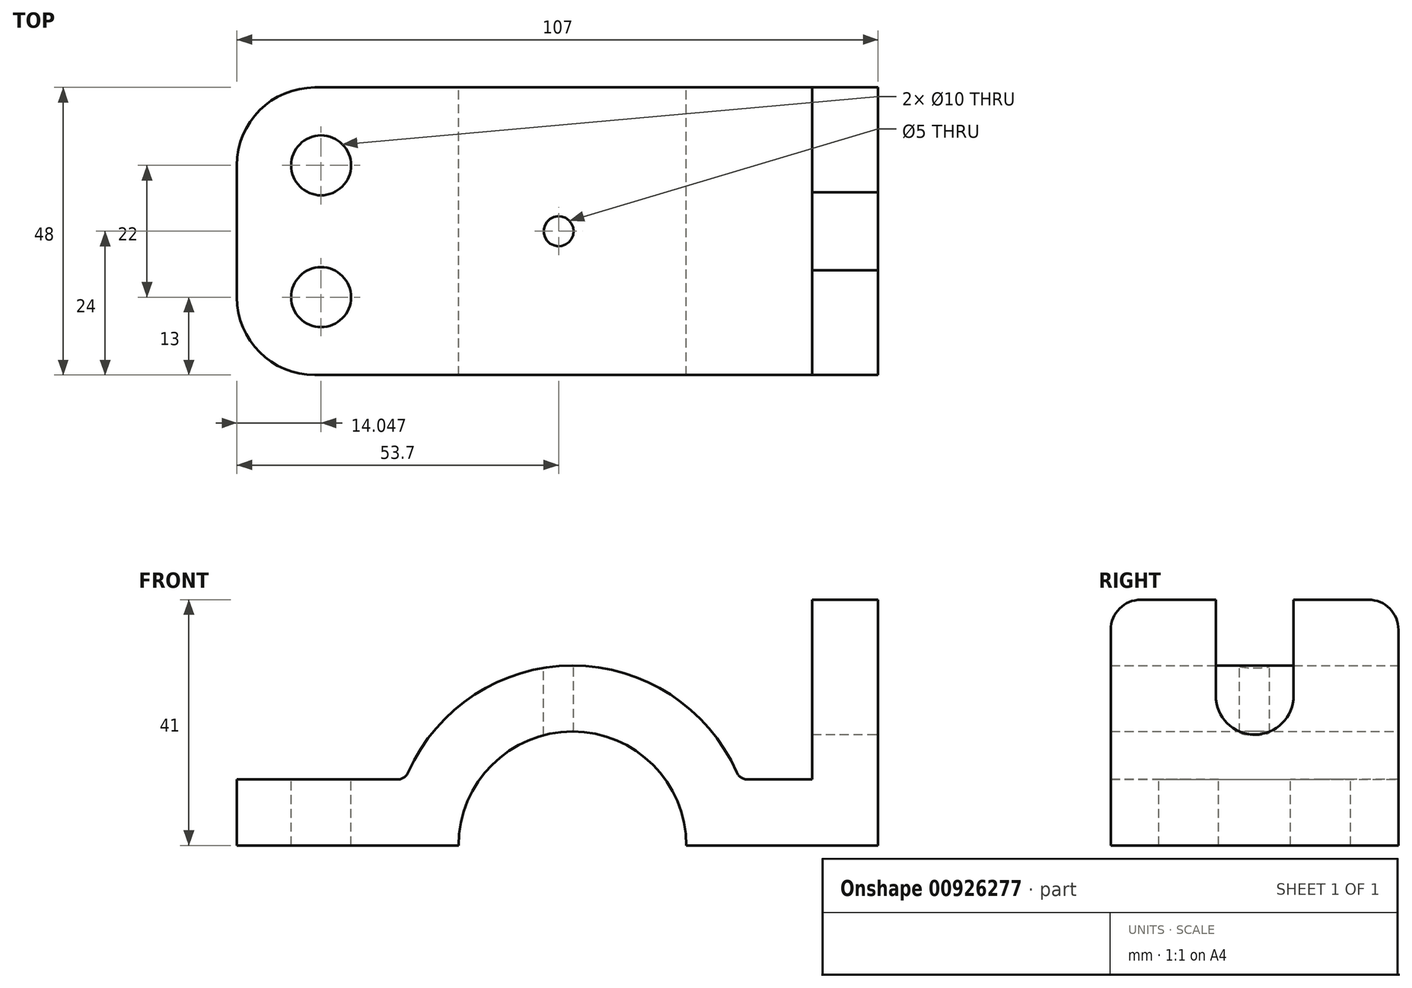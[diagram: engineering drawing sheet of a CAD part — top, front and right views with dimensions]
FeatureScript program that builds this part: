
annotation { "Feature Type Name" : "Feature", "Feature Type Description" : "" }
export const myFeature = defineFeature(function(context is Context, id is Id, definition is map)
    precondition{}
    {
        {
            var Q0;
            Q0=qCreatedBy(makeId("Front.planeOp"),FACE);
            var sketch = newSketch(context, id + "F0", { "sketchPlane" : qUnion([Q0])});
            skLineSegment(sketch, "E0.bottom", {"start": v(-53.7, -8.93) * mm, "end": v(53.3, -8.93) * mm});
            skLineSegment(sketch, "E0.top", {"start": v(-53.7, -19.93) * mm, "end": v(53.3, -19.93) * mm});
            skLineSegment(sketch, "E0.left", {"start": v(-53.7, -8.93) * mm, "end": v(-53.7, -19.93) * mm});
            skLineSegment(sketch, "E0.right", {"start": v(53.3, -8.93) * mm, "end": v(53.3, -19.93) * mm});
            skPoint(sketch, "E1", {"position": v(2.3, -19.93) * mm});
            skCircle(sketch, "E2", {"center": v(2.3, -19.93) * mm, "radius": 30 * mm});
            skCircle(sketch, "E3", {"center": v(2.3, -19.93) * mm, "radius": 19 * mm});
            skLineSegment(sketch, "E4.bottom", {"start": v(42.3, 21.07) * mm, "end": v(53.3, 21.07) * mm});
            skLineSegment(sketch, "E4.top", {"start": v(42.3, -8.93) * mm, "end": v(53.3, -8.93) * mm});
            skLineSegment(sketch, "E4.left", {"start": v(42.3, 21.07) * mm, "end": v(42.3, -8.93) * mm});
            skLineSegment(sketch, "E4.right", {"start": v(53.3, 21.07) * mm, "end": v(53.3, -8.93) * mm});
            skSolve(sketch);
        }
        {
            var Q0;
            {var subQ0=sQuery(id+"F0.wireOp",EDGE,"E0.left");Q0=makeQuery(id+"F0.imprint","IMPRINT",FACE,{"disambiguationData":[TD([[makeQuery(id+"F0.imprint","IMPRINT",EDGE,{"derivedFrom":subQ0}),1.0]])]});}
            var Q1;
            {var subQ0=sQuery(id+"F0.wireOp",EDGE,"E2");var subQ1=sQuery(id+"F0.wireOp",EDGE,"E0.bottom");var subQ2=makeQuery(id+"F0.imprint","INTERSECT",VERTEX,{"disambiguationData":[OD(0.0)],"derivedFrom":[subQ1,subQ0]});Q1=makeQuery(id+"F0.imprint","IMPRINT",FACE,{"disambiguationData":[TD([[makeQuery(id+"F0.imprint","IMPRINT",EDGE,{"disambiguationData":[TD([[subQ2,-1.0]])],"derivedFrom":subQ1}),-1.0]])]});}
            var Q2;
            {var subQ0=sQuery(id+"F0.wireOp",EDGE,"E2");var subQ1=sQuery(id+"F0.wireOp",EDGE,"E0.bottom");var subQ2=makeQuery(id+"F0.imprint","INTERSECT",VERTEX,{"disambiguationData":[OD(0.0)],"derivedFrom":[subQ1,subQ0]});Q2=makeQuery(id+"F0.imprint","IMPRINT",FACE,{"disambiguationData":[TD([[makeQuery(id+"F0.imprint","IMPRINT",EDGE,{"disambiguationData":[TD([[subQ2,-1.0]])],"derivedFrom":subQ1}),1.0]])]});}
            var Q3;
            {var subQ0=sQuery(id+"F0.wireOp",EDGE,"E2");var subQ1=sQuery(id+"F0.wireOp",EDGE,"E0.bottom");var subQ2=makeQuery(id+"F0.imprint","INTERSECT",VERTEX,{"disambiguationData":[OD(1.0)],"derivedFrom":[subQ1,subQ0]});Q3=makeQuery(id+"F0.imprint","IMPRINT",FACE,{"disambiguationData":[TD([[makeQuery(id+"F0.imprint","IMPRINT",EDGE,{"disambiguationData":[TD([[subQ2,1.0]])],"derivedFrom":subQ1}),-1.0]])]});}
            var Q4;
            {var subQ5=sQuery(id+"F0.wireOp",EDGE,"E0.right");Q4=makeQuery(id+"F0.imprint","IMPRINT",FACE,{"disambiguationData":[TD([[makeQuery(id+"F0.imprint","IMPRINT",EDGE,{"derivedFrom":subQ5}),-1.0]])]});}
            var Q5;
            Q5=makeQuery(id+"F0.imprint","IMPRINT",FACE,{"disambiguationData":[TD([[makeQuery(id+"F0.imprint","IMPRINT",EDGE,{"derivedFrom":sQuery(id+"F0.wireOp",EDGE,"E4.bottom")}),-1.0]])]});
            extrude(context, id + "F1", {"entities" : qUnion([Q0, Q1, Q2, Q3, Q4, Q5]), "endBound" : BoundingType.SYMMETRIC, "depth" : 48 * mm, "offsetDistance" : 25 * mm});
        }
        {
            var Q0;
            Q0=makeQuery(id+"F1.opExtrude","SWEPT_FACE",FACE,{"disambiguationData":[OSD([sQuery(id+"F0.wireOp",EDGE,"E0.right"),sQuery(id+"F0.wireOp",EDGE,"E4.right")])]});
            var sketch = newSketch(context, id + "F2", { "sketchPlane" : qUnion([Q0])});
            skLineSegment(sketch, "E5", {"start": v(0, 21.07) * mm, "end": v(0, -19.93) * mm, "construction": true});
            skPoint(sketch, "E6", {"position": v(0, 5.07) * mm});
            skCircle(sketch, "E7", {"center": v(0, 5.07) * mm, "radius": 6.5 * mm});
            skLineSegment(sketch, "E8", {"start": v(-6.5, 5.07) * mm, "end": v(-6.5, 21.07) * mm});
            skLineSegment(sketch, "E9", {"start": v(6.5, 5.07) * mm, "end": v(6.5, 21.07) * mm});
            skSolve(sketch);
        }
        {
            var Q0;
            {var subQ0=sQuery(id+"F2.wireOp",EDGE,"E7");var subQ1=makeQuery(id+"F2.imprint","INTERSECT",VERTEX,{"derivedFrom":[subQ0,sQuery(id+"F2.wireOp",EDGE,"E8")]});Q0=makeQuery(id+"F2.imprint","IMPRINT",FACE,{"disambiguationData":[TD([[makeQuery(id+"F2.imprint","IMPRINT",EDGE,{"disambiguationData":[TD([[subQ1,1.0]])],"derivedFrom":subQ0}),1.0]])]});}
            var Q1;
            {var subQ0=sQuery(id+"F2.wireOp",EDGE,"E8");Q1=makeQuery(id+"F2.imprint","IMPRINT",FACE,{"disambiguationData":[TD([[makeQuery(id+"F2.imprint","IMPRINT",EDGE,{"derivedFrom":subQ0}),-1.0]])]});}
            extrude(context, id + "F3", {"entities" : qUnion([Q0, Q1]), "operationType" : NewBodyOperationType.REMOVE, "oppositeDirection" : true, "depth" : 25 * mm, "offsetDistance" : 25 * mm});
        }
        {
            var Q0;
            {var subQ0=sQuery(id+"F0.wireOp",EDGE,"E0.bottom");Q0=makeQuery(id+"F1.opExtrude","SWEPT_FACE",FACE,{"disambiguationData":[OSD([subQ0]),TDD([makeQuery(id+"F0.imprint","IMPRINT",EDGE,{"disambiguationData":[TD([[makeQuery(id+"F0.imprint","INTERSECT",VERTEX,{"derivedFrom":[subQ0,sQuery(id+"F0.wireOp",EDGE,"E0.left")]}),-1.0]])],"derivedFrom":subQ0})])]});}
            var sketch = newSketch(context, id + "F4", { "sketchPlane" : qUnion([Q0])});
            skPoint(sketch, "E10", {"position": v(-39.65, -24) * mm});
            skPoint(sketch, "E11", {"position": v(-39.65, 24) * mm});
            skPoint(sketch, "E12", {"position": v(-53.7, 0) * mm});
            skPoint(sketch, "E13", {"position": v(-25.6, 0) * mm});
            skLineSegment(sketch, "E14", {"start": v(-39.65, -24) * mm, "end": v(-39.65, 24) * mm, "construction": true});
            skLineSegment(sketch, "E15", {"start": v(-53.7, 0) * mm, "end": v(-25.6, 0) * mm, "construction": true});
            skPoint(sketch, "E16", {"position": v(-39.65, -11) * mm});
            skCircle(sketch, "E17", {"center": v(-39.65, -11) * mm, "radius": 5 * mm});
            skPoint(sketch, "E18.MirrorP", {"position": v(-39.65, 11) * mm});
            skCircle(sketch, "E19.MirrorC", {"center": v(-39.65, 11) * mm, "radius": 5 * mm});
            skCircle(sketch, "E20", {"center": v(0, 0) * mm, "radius": 2.5 * mm});
            skSolve(sketch);
        }
        {
            var Q0;
            Q0 = qSketchRegion(id + "F4", true);
            extrude(context, id + "F5", {"entities" : qUnion([Q0]), "operationType" : NewBodyOperationType.REMOVE, "endBound" : BoundingType.SYMMETRIC, "oppositeDirection" : true, "depth" : 50 * mm, "offsetDistance" : 25 * mm});
        }
        {
            var Q0;
            Q0=makeQuery(id+"F1.opExtrude","CAP_EDGE",EDGE,{"disambiguationData":[OSD([sQuery(id+"F0.wireOp",EDGE,"E0.left")])],"isStart":true});
            var Q1;
            Q1=makeQuery(id+"F1.opExtrude","CAP_EDGE",EDGE,{"disambiguationData":[OSD([sQuery(id+"F0.wireOp",EDGE,"E0.left")])],"isStart":false});
            fillet(context, id + "F6", {"entities" : qUnion([Q0, Q1]), "radius" : 13 * mm, "tangentPropagation" : true, "allowEdgeOverflow" : false});
        }
        {
            var Q0;
            Q0=makeQuery(id+"F1.opExtrude","CAP_EDGE",EDGE,{"disambiguationData":[OSD([sQuery(id+"F0.wireOp",EDGE,"E4.bottom")])],"isStart":true});
            var Q1;
            Q1=makeQuery(id+"F1.opExtrude","CAP_EDGE",EDGE,{"disambiguationData":[OSD([sQuery(id+"F0.wireOp",EDGE,"E4.bottom")])],"isStart":false});
            fillet(context, id + "F7", {"entities" : qUnion([Q0, Q1]), "radius" : 5 * mm, "tangentPropagation" : true, "allowEdgeOverflow" : false});
        }
        {
            var Q0;
            {var subQ0=sQuery(id+"F0.wireOp",EDGE,"E2");var subQ1=sQuery(id+"F0.wireOp",EDGE,"E0.bottom");Q0=makeQuery(id+"F1.opExtrude","SWEPT_EDGE",EDGE,{"disambiguationData":[OSD([subQ1,subQ0]),TDD([makeQuery(id+"F0.imprint","INTERSECT",VERTEX,{"disambiguationData":[OD(1.0)],"derivedFrom":[subQ1,subQ0]})])]});}
            var Q1;
            {var subQ0=sQuery(id+"F0.wireOp",EDGE,"E2");var subQ1=sQuery(id+"F0.wireOp",EDGE,"E0.bottom");Q1=makeQuery(id+"F1.opExtrude","SWEPT_EDGE",EDGE,{"disambiguationData":[OSD([subQ1,subQ0]),TDD([makeQuery(id+"F0.imprint","INTERSECT",VERTEX,{"disambiguationData":[OD(0.0)],"derivedFrom":[subQ1,subQ0]})])]});}
            fillet(context, id + "F8", {"entities" : qUnion([Q0, Q1]), "radius" : 2 * mm, "tangentPropagation" : true, "allowEdgeOverflow" : false});
        }
    });
